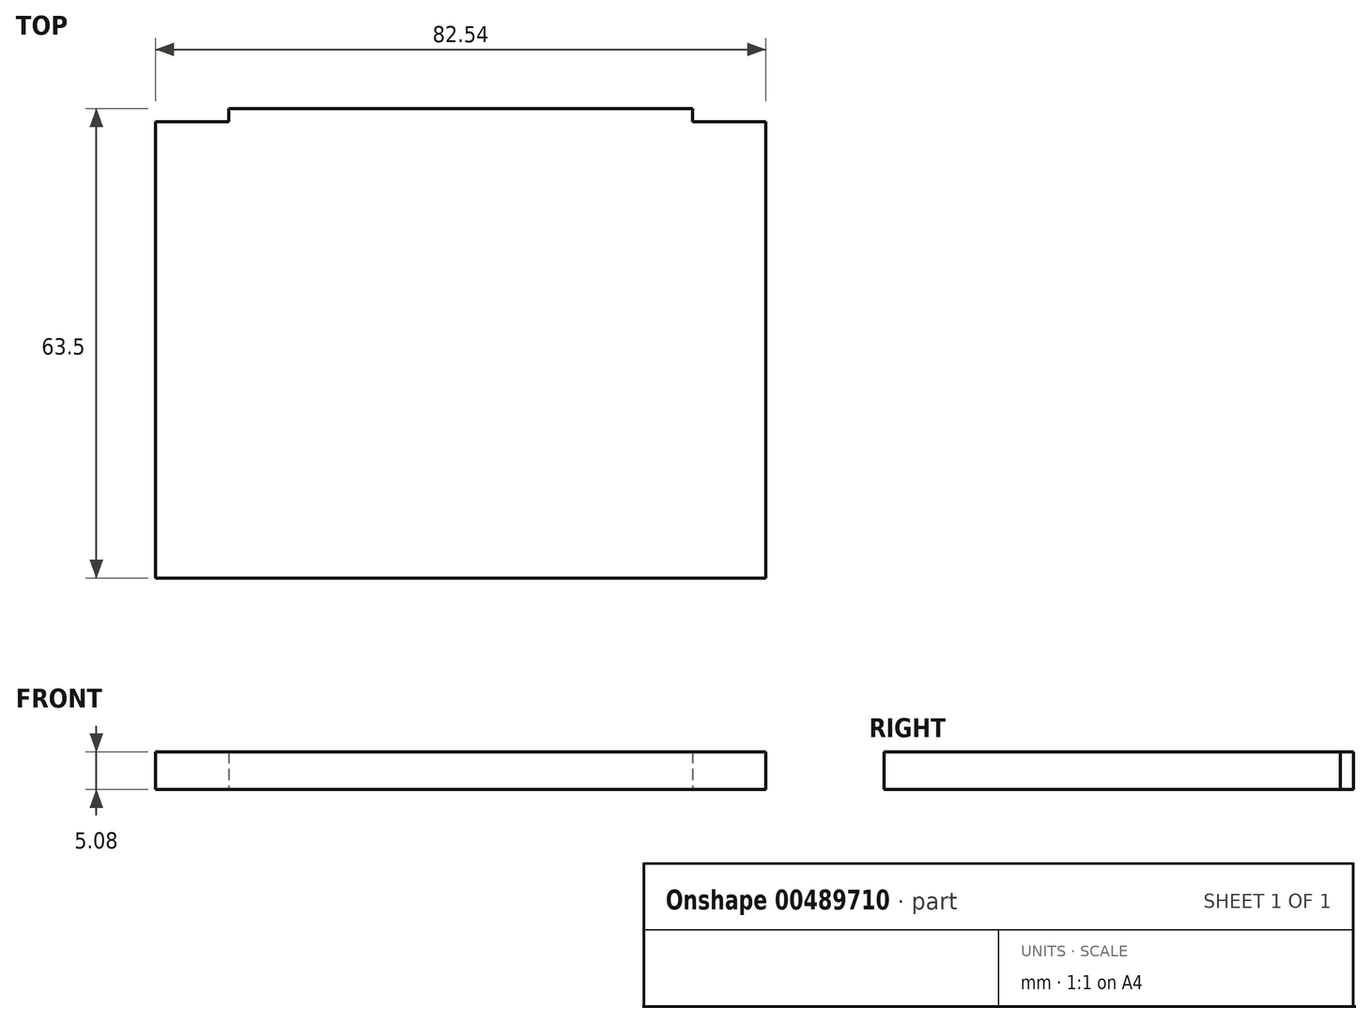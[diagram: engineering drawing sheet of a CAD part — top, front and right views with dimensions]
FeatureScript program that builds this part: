
annotation { "Feature Type Name" : "Feature", "Feature Type Description" : "" }
export const myFeature = defineFeature(function(context is Context, id is Id, definition is map)
    precondition{}
    {
        {
            var Q0;
            Q0=qCreatedBy(makeId("Top.planeOp"),FACE);
            var sketch = newSketch(context, id + "F0", { "sketchPlane" : qUnion([Q0])});
            skLineSegment(sketch, "E0.bottom", {"start": v(31.37, 31.75) * mm, "end": v(-31.37, 31.75) * mm});
            skLineSegment(sketch, "E0.top", {"start": v(41.28, -31.75) * mm, "end": v(-41.28, -31.75) * mm});
            skLineSegment(sketch, "E0.left", {"start": v(41.27, 29.97) * mm, "end": v(41.28, -31.75) * mm});
            skLineSegment(sketch, "E0.right", {"start": v(-41.28, 29.97) * mm, "end": v(-41.27, -31.75) * mm});
            skPoint(sketch, "E0.middle", {"position": v(0, 0) * mm});
            skLineSegment(sketch, "E1.top", {"start": v(-41.27, 29.97) * mm, "end": v(-31.37, 29.97) * mm});
            skLineSegment(sketch, "E1.right", {"start": v(-31.37, 31.75) * mm, "end": v(-31.37, 29.97) * mm});
            skLineSegment(sketch, "E2.MirrorCS", {"start": v(41.27, 29.97) * mm, "end": v(31.37, 29.97) * mm});
            skLineSegment(sketch, "E3.MirrorCS", {"start": v(31.37, 31.75) * mm, "end": v(31.37, 29.97) * mm});
            skPoint(sketch, "E4.orphan", {"position": v(41.27, 31.75) * mm});
            skPoint(sketch, "E5.orphan", {"position": v(-41.27, 31.75) * mm});
            skSolve(sketch);
        }
        {
            var Q0;
            Q0=makeQuery(id+"F0.imprint","IMPRINT",FACE,{"disambiguationData":[TD([[makeQuery(id+"F0.imprint","IMPRINT",EDGE,{"derivedFrom":sQuery(id+"F0.wireOp",EDGE,"E0.bottom")}),1.0]])]});
            extrude(context, id + "F1", {"entities" : qUnion([Q0]), "depth" : 5.08 * mm});
        }
    });
